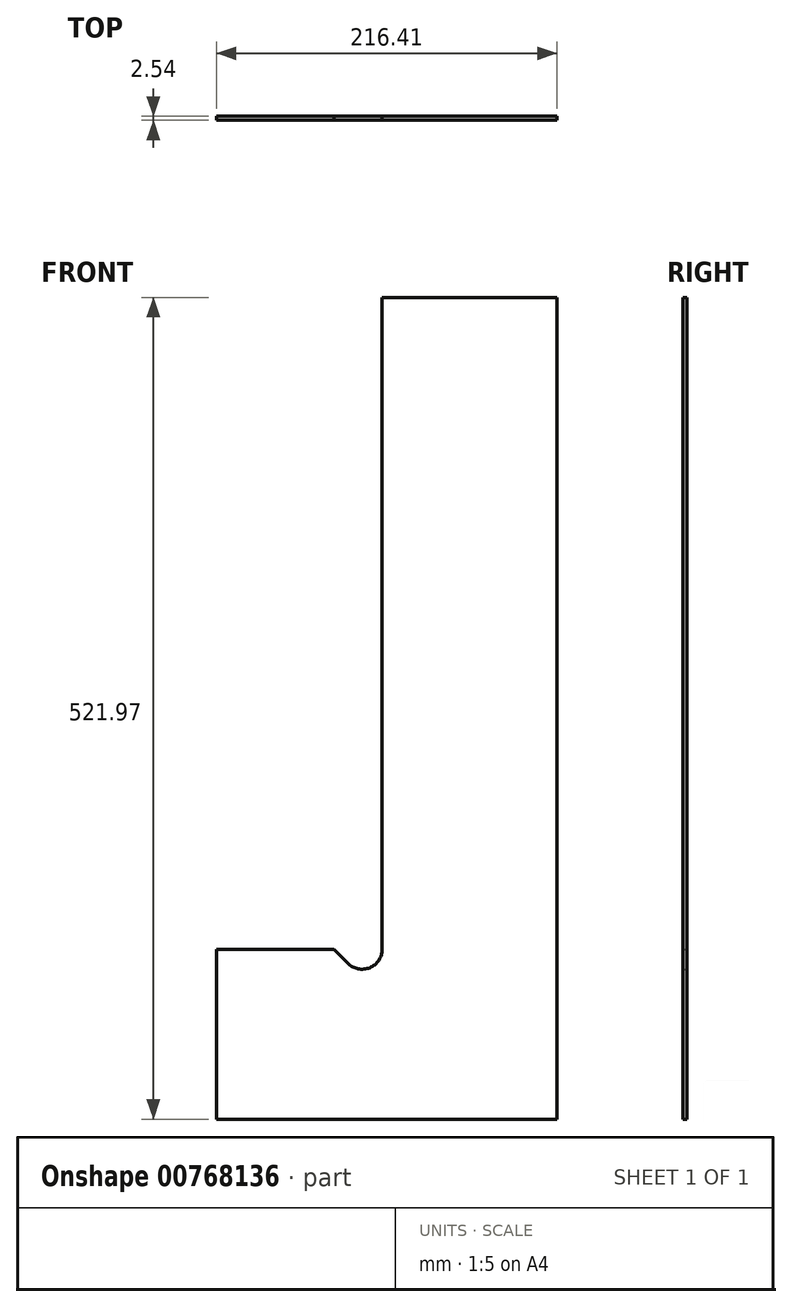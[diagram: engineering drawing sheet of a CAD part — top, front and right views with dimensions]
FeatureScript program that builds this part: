
annotation { "Feature Type Name" : "Feature", "Feature Type Description" : "" }
export const myFeature = defineFeature(function(context is Context, id is Id, definition is map)
    precondition{}
    {
        {
            var Q0;
            Q0=qCreatedBy(makeId("Front.planeOp"),FACE);
            var sketch = newSketch(context, id + "F0", { "sketchPlane" : qUnion([Q0])});
            skLineSegment(sketch, "E0", {"start": v(0, 0) * mm, "end": v(0, 595.74) * mm});
            skLineSegment(sketch, "E1", {"start": v(765.18, 521.97) * mm, "end": v(765.18, 0) * mm});
            skLineSegment(sketch, "E2", {"start": v(548.77, 0) * mm, "end": v(765.18, 0) * mm});
            skLineSegment(sketch, "E3", {"start": v(654.05, 521.97) * mm, "end": v(654.05, 107.95) * mm});
            skPoint(sketch, "E4", {"position": v(710.53, 521.97) * mm});
            skLineSegment(sketch, "E5", {"start": v(548.77, 107.95) * mm, "end": v(548.77, 0) * mm});
            skLineSegment(sketch, "E6", {"start": v(710.53, 521.97) * mm, "end": v(654.05, 521.97) * mm});
            skLineSegment(sketch, "E7", {"start": v(710.53, 521.97) * mm, "end": v(765.18, 521.97) * mm});
            skPoint(sketch, "E8", {"position": v(647.82, 95.25) * mm});
            skArc(sketch, "E9", {"start": v(632.37, 98.97) * mm, "mid": v(646.21, 96.22) * mm, "end": v(654.05, 107.95) * mm});
            skLineSegment(sketch, "E10.trimOffspring", {"start": v(623.39, 107.95) * mm, "end": v(548.77, 107.95) * mm});
            skLineSegment(sketch, "E11", {"start": v(632.37, 98.97) * mm, "end": v(623.39, 107.95) * mm});
            skArc(sketch, "E12.MirrorCS", {"start": v(-632.37, 98.97) * mm, "mid": v(-646.21, 96.22) * mm, "end": v(-654.05, 107.95) * mm});
            skLineSegment(sketch, "E13.MirrorCS", {"start": v(-632.37, 98.97) * mm, "end": v(-623.39, 107.95) * mm});
            skLineSegment(sketch, "E14.MirrorCS", {"start": v(-710.53, 521.97) * mm, "end": v(-765.18, 521.97) * mm});
            skLineSegment(sketch, "E15.MirrorCS", {"start": v(-710.53, 521.97) * mm, "end": v(-654.05, 521.97) * mm});
            skLineSegment(sketch, "E16.MirrorCS", {"start": v(-654.05, 521.97) * mm, "end": v(-654.05, 107.95) * mm});
            skLineSegment(sketch, "E17.MirrorCS", {"start": v(-623.39, 107.95) * mm, "end": v(-548.77, 107.95) * mm});
            skLineSegment(sketch, "E18.MirrorCS", {"start": v(-548.77, 0) * mm, "end": v(-765.18, 0) * mm});
            skLineSegment(sketch, "E19.MirrorCS", {"start": v(-765.18, 521.97) * mm, "end": v(-765.18, 0) * mm});
            skLineSegment(sketch, "E20.MirrorCS", {"start": v(-548.77, 107.95) * mm, "end": v(-548.77, 0) * mm});
            skPoint(sketch, "E21.MirrorP", {"position": v(-710.53, 521.97) * mm});
            skSolve(sketch);
        }
        {
            var Q0;
            Q0=makeQuery(id+"F0.imprint","IMPRINT",FACE,{"disambiguationData":[TD([[makeQuery(id+"F0.imprint","IMPRINT",EDGE,{"derivedFrom":sQuery(id+"F0.wireOp",EDGE,"E12.MirrorCS")}),1.0]])]});
            var Q1;
            Q1=makeQuery(id+"F0.imprint","IMPRINT",FACE,{"disambiguationData":[TD([[makeQuery(id+"F0.imprint","IMPRINT",EDGE,{"derivedFrom":sQuery(id+"F0.wireOp",EDGE,"E1")}),-1.0]])]});
            extrude(context, id + "F1", {"entities" : qUnion([Q0, Q1]), "depth" : 2.54 * mm, "offsetDistance" : 25.4 * mm});
        }
    });
